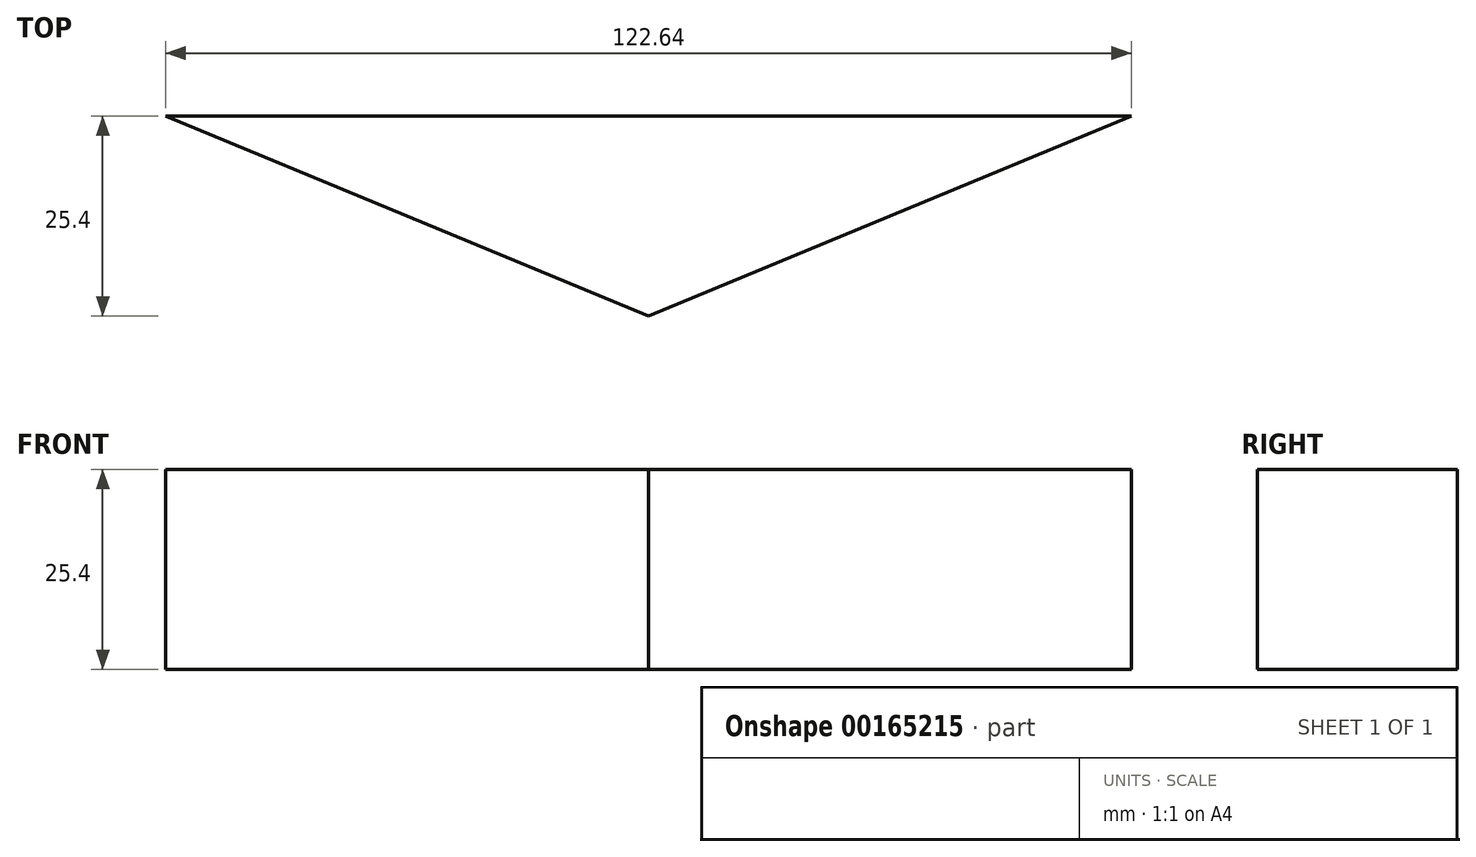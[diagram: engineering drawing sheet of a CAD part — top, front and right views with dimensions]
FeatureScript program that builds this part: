
annotation { "Feature Type Name" : "Feature", "Feature Type Description" : "" }
export const myFeature = defineFeature(function(context is Context, id is Id, definition is map)
    precondition{}
    {
        {
            var Q0;
            Q0=qCreatedBy(makeId("Top.planeOp"),FACE);
            var sketch = newSketch(context, id + "F0", { "sketchPlane" : qUnion([Q0])});
            skLineSegment(sketch, "E0", {"start": v(0, 0) * mm, "end": v(61.32, 25.4) * mm});
            skLineSegment(sketch, "E1", {"start": v(61.32, 25.4) * mm, "end": v(-61.32, 25.4) * mm});
            skLineSegment(sketch, "E2", {"start": v(-61.32, 25.4) * mm, "end": v(0, 0) * mm});
            skLineSegment(sketch, "E3", {"start": v(0, 25.4) * mm, "end": v(0, 0) * mm, "construction": true});
            skSolve(sketch);
        }
        {
            var Q0;
            Q0=qSketchRegion(id+"F0",true);
            extrude(context, id + "F1", {"entities" : qUnion([Q0]), "depth" : 25.4 * mm});
        }
    });
